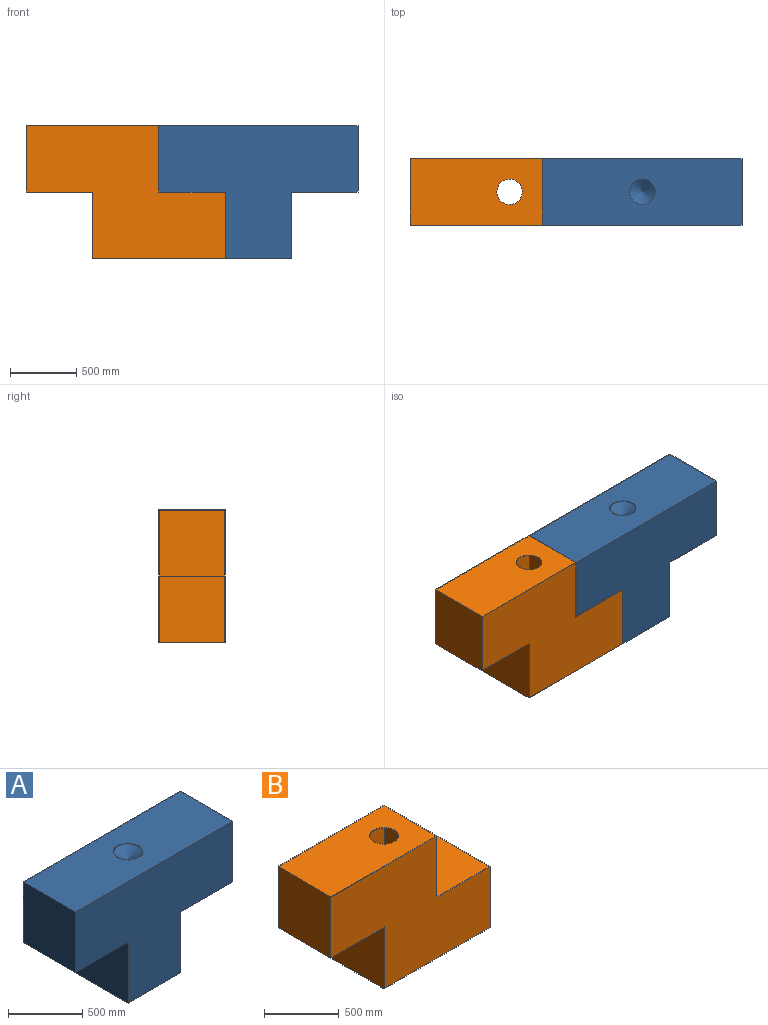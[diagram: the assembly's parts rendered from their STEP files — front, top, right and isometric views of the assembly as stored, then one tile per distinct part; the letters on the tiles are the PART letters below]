
ASSEMBLY  parts=2 mates=1
PART A: 23 faces, bbox 1500x500x1000 mm
  f0: plane 500x500mm, normal (0,0,-1), area 9900mm2, adj f2,f3,f4,f5,f13,f14,f15,f16
  f1: plane 1500x500mm, normal (0,0,1), area 721047.1mm2, adj f4,f5,f6,f9,f11
  f2: plane 500x500mm, normal (-1,0,0), area 250000mm2, adj f0,f4,f5,f7
  f3: plane 500x500mm, normal (1,0,0), area 250000mm2, adj f0,f4,f5,f8
  f4: plane 1500x1000mm, normal (0,-1,0), area 1000000mm2, adj f0,f1,f2,f3,f6,f7,f8,f9
  f5: plane 1500x1000mm, normal (0,1,0), area 1000000mm2, adj f0,f1,f2,f3,f6,f7,f8,f9
  f6: plane 500x500mm, normal (-1,0,0), area 250000mm2, adj f1,f4,f5,f7
  f7: plane 500x500mm, normal (0,0,-1), area 250000mm2, adj f2,f4,f5,f6
  f8: plane 500x500mm, normal (0,0,-1), area 250000mm2, adj f3,f4,f5,f9
  f9: plane 500x500mm, normal (1,0,0), area 250000mm2, adj f1,f4,f5,f8
  f10: cone r=0mm half-angle=59deg, axis (0,0,1), area 33777.4mm2, adj f11
  f11: cylinder r=96mm len=192mm, axis (0,0,1), area 3015.9mm2, adj f1,f10
  f12: plane 1490x490mm, normal (0,0,-1), area 698052.6mm2, adj f15,f16,f17,f20,f22
  f13: plane 505x490mm, normal (1,0,0), area 247450mm2, adj f0,f15,f16,f18
  f14: plane 505x490mm, normal (-1,0,0), area 247450mm2, adj f0,f15,f16,f19
  f15: plane 1490x995mm, normal (0,1,0), area 977550mm2, adj f0,f12,f13,f14,f17,f18,f19,f20
  f16: plane 1490x995mm, normal (0,-1,0), area 977550mm2, adj f0,f12,f13,f14,f17,f18,f19,f20
  f17: plane 490x490mm, normal (1,0,0), area 240100mm2, adj f12,f15,f16,f18
  f18: plane 500x490mm, normal (0,0,1), area 245000mm2, adj f13,f15,f16,f17
  f19: plane 500x490mm, normal (0,0,1), area 245000mm2, adj f14,f15,f16,f20
  f20: plane 490x490mm, normal (-1,0,0), area 240100mm2, adj f12,f15,f16,f19
  f21: cone r=2.58mm half-angle=59deg, axis (0,0,1), area 37387.6mm2, adj f22
  f22: cylinder r=101mm len=202mm, axis (0,0,1), area 1795.2mm2, adj f12,f21
PART B: 20 faces, bbox 1500x500x1000 mm
  f0: plane 1000x500mm, normal (0,0,-1), area 14900mm2, adj f4,f5,f8,f9,f13,f14,f17,f18
  f1: plane 500x500mm, normal (0,0,-1), area 7450mm2, adj f4,f5,f6,f9,f13,f14,f15
  f2: plane 1000x500mm, normal (0,0,1), area 471047.1mm2, adj f3,f4,f5,f6,f19
  f3: plane 500x500mm, normal (1,0,0), area 250000mm2, adj f2,f4,f5,f7
  f4: plane 1500x1000mm, normal (0,-1,0), area 1000000mm2, adj f0,f1,f2,f3,f6,f7,f8,f9
  f5: plane 1500x1000mm, normal (0,1,0), area 1000000mm2, adj f0,f1,f2,f3,f6,f7,f8,f9
  f6: plane 500x500mm, normal (-1,0,0), area 250000mm2, adj f1,f2,f4,f5
  f7: plane 500x500mm, normal (0,0,1), area 250000mm2, adj f3,f4,f5,f8
  f8: plane 500x500mm, normal (1,0,0), area 250000mm2, adj f0,f4,f5,f7
  f9: plane 500x500mm, normal (-1,0,0), area 250000mm2, adj f0,f1,f4,f5,f10
  f10: plane 490x5mm, normal (0,0,1), area 2450mm2, adj f9,f13,f14,f18
  f11: plane 990x490mm, normal (0,0,-1), area 456147.1mm2, adj f12,f13,f14,f15,f19
  f12: plane 500x490mm, normal (-1,0,0), area 245000mm2, adj f11,f13,f14,f16
  f13: plane 1490x995mm, normal (0,1,0), area 982550mm2, adj f0,f1,f10,f11,f12,f15,f16,f17
  f14: plane 1490x995mm, normal (0,-1,0), area 982550mm2, adj f0,f1,f10,f11,f12,f15,f16,f17
  f15: plane 495x490mm, normal (1,0,0), area 242550mm2, adj f1,f11,f13,f14
  f16: plane 500x490mm, normal (0,0,-1), area 245000mm2, adj f12,f13,f14,f17
  f17: plane 495x490mm, normal (-1,0,0), area 242550mm2, adj f0,f13,f14,f16
  f18: plane 500x490mm, normal (1,0,0), area 245000mm2, adj f0,f10,f13,f14
  f19: cylinder r=96mm len=192mm, axis (0,0,1), area 3015.9mm2, adj f2,f11
PLACE A t=(0,0,-245)mm
PLACE B t=(-1000,0,-245)mm
MATE slider A.f2 <-> B.f8  axis (-1,0,0) through (-250,0,-745)mm
